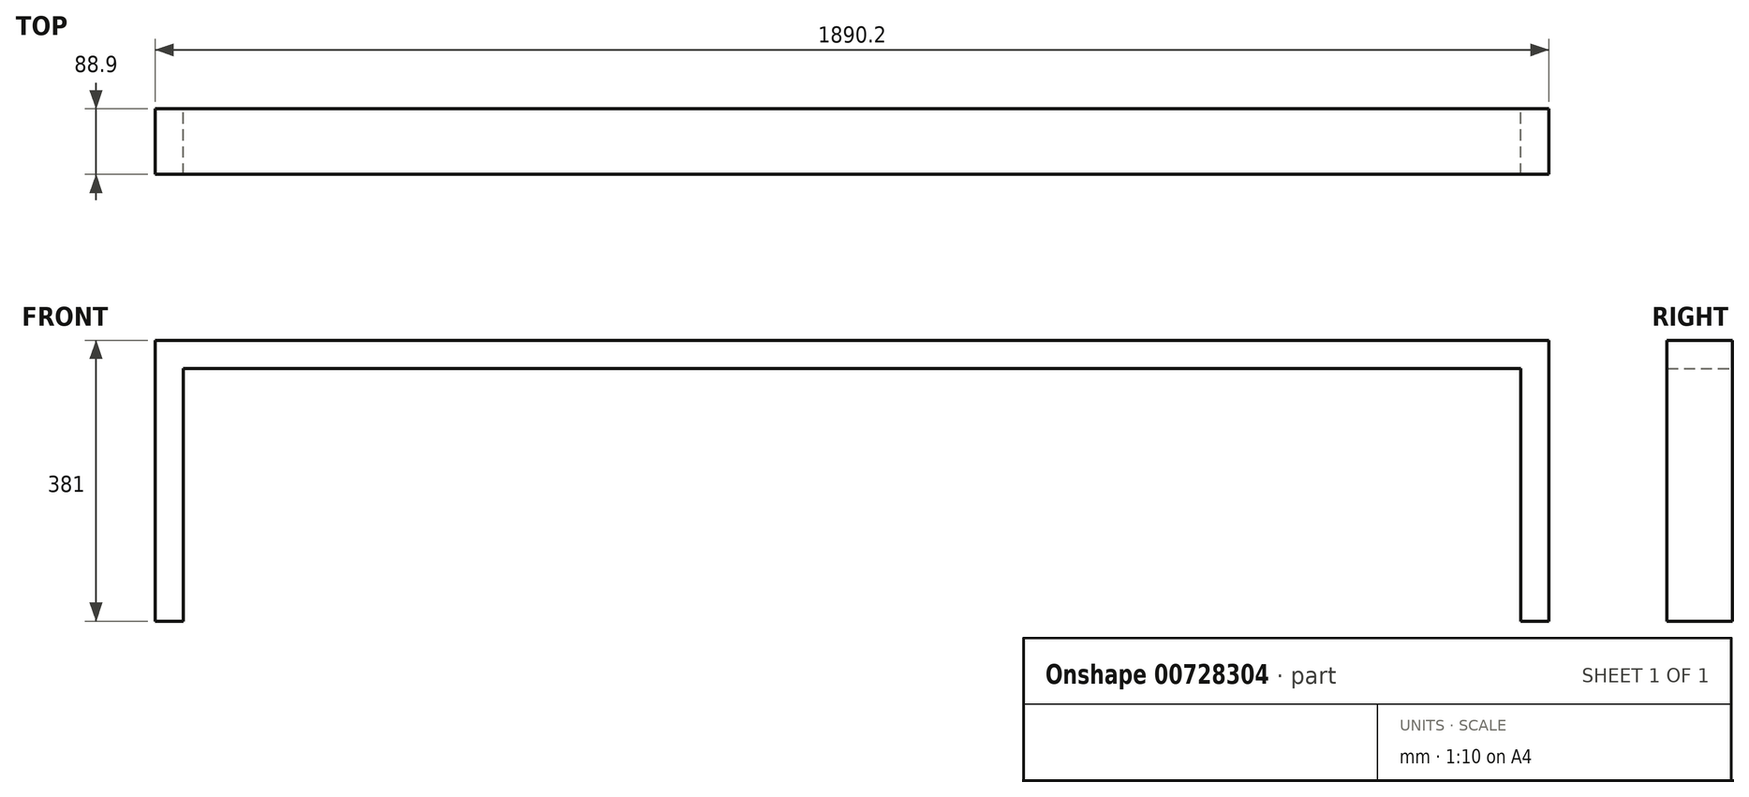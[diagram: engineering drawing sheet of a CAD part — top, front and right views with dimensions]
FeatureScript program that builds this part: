
annotation { "Feature Type Name" : "Feature", "Feature Type Description" : "" }
export const myFeature = defineFeature(function(context is Context, id is Id, definition is map)
    precondition{}
    {
        {
            var Q0;
            Q0=qCreatedBy(makeId("Front.planeOp"),FACE);
            var sketch = newSketch(context, id + "F0", { "sketchPlane" : qUnion([Q0])});
            skLineSegment(sketch, "E0", {"start": v(-74.39, 0) * mm, "end": v(1815.81, 0) * mm});
            skLineSegment(sketch, "E1", {"start": v(1815.81, 0) * mm, "end": v(1815.81, -381) * mm});
            skLineSegment(sketch, "E2", {"start": v(1815.81, -381) * mm, "end": v(1777.71, -381) * mm});
            skLineSegment(sketch, "E3", {"start": v(1777.71, -381) * mm, "end": v(1777.71, -38.1) * mm});
            skLineSegment(sketch, "E4", {"start": v(-74.39, 0) * mm, "end": v(-74.39, -381) * mm});
            skLineSegment(sketch, "E5", {"start": v(-74.39, -381) * mm, "end": v(-36.29, -381) * mm});
            skLineSegment(sketch, "E6", {"start": v(-36.29, -381) * mm, "end": v(-36.29, -38.1) * mm});
            skLineSegment(sketch, "E7", {"start": v(-36.29, -38.1) * mm, "end": v(1777.71, -38.1) * mm});
            skSolve(sketch);
        }
        {
            var Q0;
            Q0=qSketchRegion(id+"F0",true);
            extrude(context, id + "F1", {"entities" : qUnion([Q0]), "depth" : 88.9 * mm, "offsetDistance" : 25.4 * mm});
        }
    });
